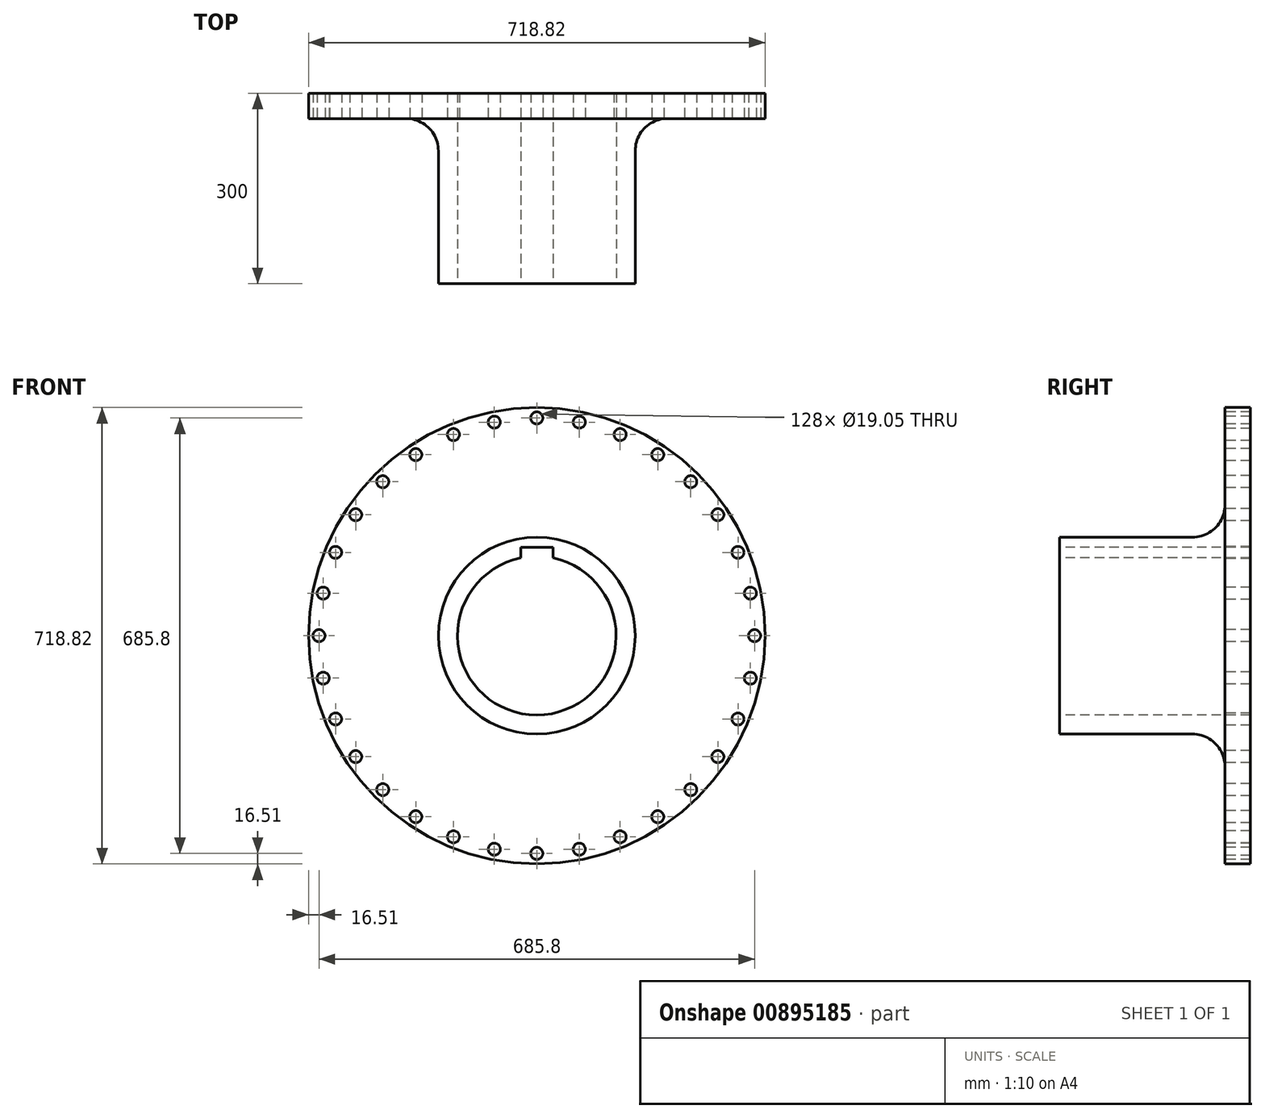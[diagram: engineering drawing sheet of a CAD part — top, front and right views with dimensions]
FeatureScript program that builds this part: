
annotation { "Feature Type Name" : "Feature", "Feature Type Description" : "" }
export const myFeature = defineFeature(function(context is Context, id is Id, definition is map)
    precondition{}
    {
        {
            var Q0;
            Q0=qCreatedBy(makeId("Front.planeOp"),FACE);
            var sketch = newSketch(context, id + "F0", { "sketchPlane" : qUnion([Q0])});
            skCircle(sketch, "E0", {"center": v(0, 0) * mm, "radius": 359.41 * mm});
            skSolve(sketch);
        }
        {
            var Q0;
            Q0 = qSketchRegion(id + "F0", true);
            extrude(context, id + "F1", {"entities" : qUnion([Q0]), "depth" : 300 * mm, "offsetDistance" : 25.4 * mm});
        }
        {
            var Q0;
            Q0=makeQuery(id+"F1.opExtrude","CAP_FACE",FACE,{"disambiguationData":[OSD([sQuery(id+"F0.wireOp",EDGE,"E0")])],"isStart":false});
            var sketch = newSketch(context, id + "F2", { "sketchPlane" : qUnion([Q0])});
            skCircle(sketch, "E1", {"center": v(0, 0) * mm, "radius": 155 * mm});
            skCircle(sketch, "E2", {"center": v(0, 0) * mm, "radius": 504.34 * mm});
            skSolve(sketch);
        }
        {
            var Q0;
            Q0 = qSketchRegion(id + "F2", true);
            extrude(context, id + "F3", {"entities" : qUnion([Q0]), "operationType" : NewBodyOperationType.REMOVE, "oppositeDirection" : true, "depth" : 260 * mm, "offsetDistance" : 25.4 * mm});
        }
        {
            var Q0;
            Q0=makeQuery(id+"F3.boolean.opBoolean","COPY",EDGE,{"derivedFrom":makeQuery(id+"F3.opExtrude","CAP_EDGE",EDGE,{"disambiguationData":[OSD([sQuery(id+"F2.wireOp",EDGE,"E1")])],"isStart":false})});
            fillet(context, id + "F4", {"entities" : qUnion([Q0]), "radius" : 50.8 * mm, "tangentPropagation" : true, "allowEdgeOverflow" : false});
        }
        {
            var Q0;
            Q0=makeQuery(id+"F1.opExtrude","CAP_FACE",FACE,{"disambiguationData":[OSD([sQuery(id+"F0.wireOp",EDGE,"E0")])],"isStart":false});
            var sketch = newSketch(context, id + "F5", { "sketchPlane" : qUnion([Q0])});
            skCircle(sketch, "E3", {"center": v(0, 0) * mm, "radius": 125 * mm});
            skSolve(sketch);
        }
        {
            var Q0;
            Q0 = qSketchRegion(id + "F5", true);
            extrude(context, id + "F6", {"entities" : qUnion([Q0]), "operationType" : NewBodyOperationType.REMOVE, "oppositeDirection" : true, "depth" : 708.66 * mm, "offsetDistance" : 25.4 * mm});
        }
        {
            var Q0;
            Q0=makeQuery(id+"F3.boolean.opBoolean","COPY",FACE,{"derivedFrom":makeQuery(id+"F3.opExtrude","CAP_FACE",FACE,{"disambiguationData":[OSD([sQuery(id+"F2.wireOp",EDGE,"E1"),sQuery(id+"F2.wireOp",EDGE,"E2")])],"isStart":false})});
            var sketch = newSketch(context, id + "F7", { "sketchPlane" : qUnion([Q0])});
            skLineSegment(sketch, "E4", {"start": v(0, 0) * mm, "end": v(0, 359.41) * mm, "construction": true});
            skCircle(sketch, "E5", {"center": v(0, 0) * mm, "radius": 342.9 * mm, "construction": true});
            skCircle(sketch, "E6", {"center": v(0, 342.9) * mm, "radius": 9.53 * mm});
            skCircle(sketch, "E7.1.0", {"center": v(-66.9, 336.31) * mm, "radius": 9.53 * mm});
            skCircle(sketch, "E7.2.0", {"center": v(-131.22, 316.8) * mm, "radius": 9.52 * mm});
            skCircle(sketch, "E8.1.3.0", {"center": v(-190.5, 285.11) * mm, "radius": 9.53 * mm});
            skCircle(sketch, "E8.1.4.0", {"center": v(-242.47, 242.47) * mm, "radius": 9.53 * mm});
            skCircle(sketch, "E8.1.5.0", {"center": v(-285.11, 190.5) * mm, "radius": 9.53 * mm});
            skCircle(sketch, "E8.1.6.0", {"center": v(-316.8, 131.22) * mm, "radius": 9.53 * mm});
            skCircle(sketch, "E8.1.7.0", {"center": v(-336.31, 66.9) * mm, "radius": 9.53 * mm});
            skCircle(sketch, "E8.1.8.0", {"center": v(-342.9, 0) * mm, "radius": 9.53 * mm});
            skCircle(sketch, "E8.1.9.0", {"center": v(-336.31, -66.9) * mm, "radius": 9.53 * mm});
            skCircle(sketch, "E8.1.10.0", {"center": v(-316.8, -131.22) * mm, "radius": 9.53 * mm});
            skCircle(sketch, "E8.1.11.0", {"center": v(-285.11, -190.5) * mm, "radius": 9.53 * mm});
            skCircle(sketch, "E8.1.12.0", {"center": v(-242.47, -242.47) * mm, "radius": 9.53 * mm});
            skCircle(sketch, "E8.1.13.0", {"center": v(-190.5, -285.11) * mm, "radius": 9.53 * mm});
            skCircle(sketch, "E8.1.14.0", {"center": v(-131.22, -316.8) * mm, "radius": 9.53 * mm});
            skCircle(sketch, "E8.1.15.0", {"center": v(-66.9, -336.31) * mm, "radius": 9.53 * mm});
            skCircle(sketch, "E8.1.16.0", {"center": v(0, -342.9) * mm, "radius": 9.53 * mm});
            skCircle(sketch, "E8.1.17.0", {"center": v(66.9, -336.31) * mm, "radius": 9.53 * mm});
            skCircle(sketch, "E8.1.18.0", {"center": v(131.22, -316.8) * mm, "radius": 9.53 * mm});
            skCircle(sketch, "E8.1.19.0", {"center": v(190.5, -285.11) * mm, "radius": 9.53 * mm});
            skCircle(sketch, "E8.1.20.0", {"center": v(242.47, -242.47) * mm, "radius": 9.53 * mm});
            skCircle(sketch, "E8.1.21.0", {"center": v(285.11, -190.5) * mm, "radius": 9.53 * mm});
            skCircle(sketch, "E8.1.22.0", {"center": v(316.8, -131.22) * mm, "radius": 9.53 * mm});
            skCircle(sketch, "E8.1.23.0", {"center": v(336.31, -66.9) * mm, "radius": 9.53 * mm});
            skCircle(sketch, "E8.1.24.0", {"center": v(342.9, 0) * mm, "radius": 9.53 * mm});
            skCircle(sketch, "E8.1.25.0", {"center": v(336.31, 66.9) * mm, "radius": 9.53 * mm});
            skCircle(sketch, "E8.1.26.0", {"center": v(316.8, 131.22) * mm, "radius": 9.53 * mm});
            skCircle(sketch, "E8.1.27.0", {"center": v(285.11, 190.5) * mm, "radius": 9.53 * mm});
            skCircle(sketch, "E8.1.28.0", {"center": v(242.47, 242.47) * mm, "radius": 9.53 * mm});
            skCircle(sketch, "E8.1.29.0", {"center": v(190.5, 285.11) * mm, "radius": 9.53 * mm});
            skCircle(sketch, "E8.1.30.0", {"center": v(131.22, 316.8) * mm, "radius": 9.53 * mm});
            skCircle(sketch, "E8.1.31.0", {"center": v(66.9, 336.31) * mm, "radius": 9.53 * mm});
            skSolve(sketch);
        }
        {
            var Q0;
            Q0 = qSketchRegion(id + "F7", true);
            extrude(context, id + "F8", {"entities" : qUnion([Q0]), "operationType" : NewBodyOperationType.REMOVE, "oppositeDirection" : true, "depth" : 109.22 * mm, "offsetDistance" : 25.4 * mm});
        }
        {
            var Q0;
            Q0=makeQuery(id+"F1.opExtrude","CAP_FACE",FACE,{"disambiguationData":[OSD([sQuery(id+"F0.wireOp",EDGE,"E0")])],"isStart":false});
            var sketch = newSketch(context, id + "F9", { "sketchPlane" : qUnion([Q0])});
            skLineSegment(sketch, "E9", {"start": v(0, 0) * mm, "end": v(0, 595.67) * mm});
            skLineSegment(sketch, "E10.bottom", {"start": v(-25.4, 0) * mm, "end": v(25.4, 0) * mm});
            skLineSegment(sketch, "E10.top", {"start": v(-25.4, 139.05) * mm, "end": v(25.4, 139.05) * mm});
            skLineSegment(sketch, "E10.left", {"start": v(-25.4, 139.05) * mm, "end": v(-25.4, 0) * mm});
            skLineSegment(sketch, "E10.right", {"start": v(25.4, 139.05) * mm, "end": v(25.4, 0) * mm});
            skSolve(sketch);
        }
        {
            var Q0;
            {var subQ0=sQuery(id+"F9.wireOp",EDGE,"E10.bottom");var subQ1=sQuery(id+"F9.wireOp",EDGE,"E9");var subQ2=makeQuery(id+"F9.imprint","INTERSECT",VERTEX,{"derivedFrom":[subQ1,subQ0]});Q0=makeQuery(id+"F9.imprint","IMPRINT",FACE,{"disambiguationData":[TD([[makeQuery(id+"F9.imprint","IMPRINT",EDGE,{"disambiguationData":[TD([[subQ2,-1.0]])],"derivedFrom":subQ1}),-1.0]])]});}
            var Q1;
            {var subQ0=sQuery(id+"F9.wireOp",EDGE,"E10.top");var subQ1=sQuery(id+"F9.wireOp",EDGE,"E9");var subQ2=makeQuery(id+"F9.imprint","INTERSECT",VERTEX,{"derivedFrom":[subQ1,subQ0]});Q1=makeQuery(id+"F9.imprint","IMPRINT",FACE,{"disambiguationData":[TD([[makeQuery(id+"F9.imprint","IMPRINT",EDGE,{"disambiguationData":[TD([[subQ2,1.0]])],"derivedFrom":subQ1}),1.0]])]});}
            var Q2;
            {var subQ0=sQuery(id+"F9.wireOp",EDGE,"E10.bottom");var subQ1=sQuery(id+"F9.wireOp",EDGE,"E9");var subQ2=makeQuery(id+"F9.imprint","INTERSECT",VERTEX,{"derivedFrom":[subQ1,subQ0]});Q2=makeQuery(id+"F9.imprint","IMPRINT",FACE,{"disambiguationData":[TD([[makeQuery(id+"F9.imprint","IMPRINT",EDGE,{"disambiguationData":[TD([[subQ2,-1.0]])],"derivedFrom":subQ1}),1.0]])]});}
            var Q3;
            {var subQ0=sQuery(id+"F9.wireOp",EDGE,"E10.top");var subQ1=sQuery(id+"F9.wireOp",EDGE,"E9");var subQ2=makeQuery(id+"F9.imprint","INTERSECT",VERTEX,{"derivedFrom":[subQ1,subQ0]});Q3=makeQuery(id+"F9.imprint","IMPRINT",FACE,{"disambiguationData":[TD([[makeQuery(id+"F9.imprint","IMPRINT",EDGE,{"disambiguationData":[TD([[subQ2,1.0]])],"derivedFrom":subQ1}),-1.0]])]});}
            extrude(context, id + "F10", {"entities" : qUnion([Q0, Q1, Q2, Q3]), "operationType" : NewBodyOperationType.REMOVE, "oppositeDirection" : true, "depth" : 340.87 * mm, "offsetDistance" : 25.4 * mm});
        }
    });
